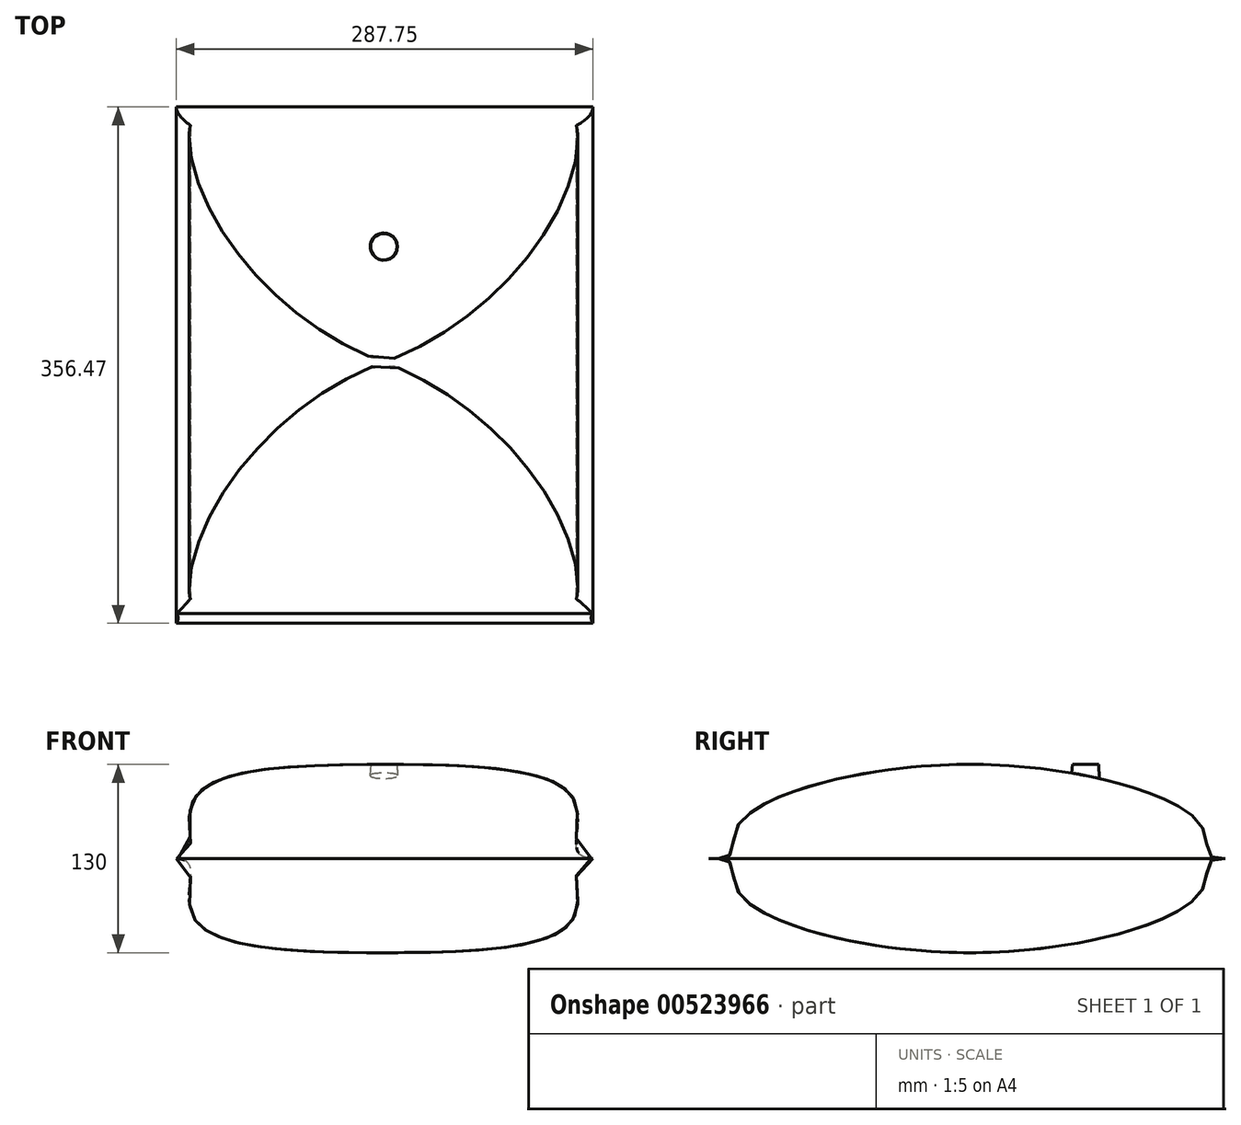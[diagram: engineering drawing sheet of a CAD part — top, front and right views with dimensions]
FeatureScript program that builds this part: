
annotation { "Feature Type Name" : "Feature", "Feature Type Description" : "" }
export const myFeature = defineFeature(function(context is Context, id is Id, definition is map)
    precondition{}
    {
        {
            var Q0;
            Q0=qCreatedBy(makeId("Right.planeOp"),FACE);
            var sketch = newSketch(context, id + "F0", { "sketchPlane" : qUnion([Q0])});
            skLineSegment(sketch, "E0", {"start": v(0, 0) * mm, "end": v(300, 0) * mm});
            skLineSegment(sketch, "E1", {"start": v(0, 0) * mm, "end": v(360, 0) * mm, "construction": true});
            skLineSegment(sketch, "E2", {"start": v(180, 0) * mm, "end": v(180, 198.32) * mm, "construction": true});
            skFitSpline(sketch, "E3", {"points": [v(0, 0) * mm, v(15, 3) * mm, v(19.87, 22.56) * mm, v(180, 65) * mm, v(340.13, 22.56) * mm, v(345, 3) * mm, v(360, 0) * mm], "startDerivative": vector(169.87, -8.58) * mm, "endDerivative": vector(272.86, 0) * mm});
            skFitSpline(sketch, "E4.MirrorCS", {"points": [v(0, 0) * mm, v(15, -3) * mm, v(19.87, -22.56) * mm, v(180, -65) * mm, v(340.13, -22.56) * mm, v(345, -3) * mm, v(360, 0) * mm], "startDerivative": vector(169.87, 8.58) * mm, "endDerivative": vector(272.86, 0) * mm});
            skSolve(sketch);
        }
        {
            var Q0;
            Q0 = qSketchRegion(id + "F0", true);
            extrude(context, id + "F1", {"entities" : qUnion([Q0]), "depth" : 300 * mm, "offsetDistance" : 25 * mm, "symmetric" : true});
        }
        {
            var Q0;
            Q0=qCreatedBy(makeId("Top.planeOp"),FACE);
            var sketch = newSketch(context, id + "F2", { "sketchPlane" : qUnion([Q0])});
            skLineSegment(sketch, "E5", {"start": v(0, -42.79) * mm, "end": v(0, 484.8) * mm, "construction": true});
            skCircle(sketch, "E6", {"center": v(0, 260) * mm, "radius": 12.5 * mm});
            skSolve(sketch);
        }
        {
            var Q0;
            Q0 = qSketchRegion(id + "F2", true);
            extrude(context, id + "F3", {"entities" : qUnion([Q0]), "operationType" : NewBodyOperationType.ADD, "depth" : 65 * mm, "offsetDistance" : 25 * mm, "hasDraft" : true, "draftAngle" : 3 * degree, "draftPullDirection" : true});
        }
        {
            var Q0;
            Q0=qCreatedBy(makeId("Front.planeOp"),FACE);
            var sketch = newSketch(context, id + "F4", { "sketchPlane" : qUnion([Q0])});
            skLineSegment(sketch, "E7", {"start": v(0, 0) * mm, "end": v(0, 80) * mm, "construction": true});
            skLineSegment(sketch, "E8.0", {"start": v(150, 0) * mm, "end": v(-150, 0) * mm, "construction": true});
            skPoint(sketch, "E9.4.internal.snap0", {"position": v(0, 40) * mm});
            skFitSpline(sketch, "E9", {"points": [v(-150, 0) * mm, v(-135, 3.26) * mm, v(-131.8, 40) * mm, v(0, 65) * mm, v(131.8, 40) * mm, v(135, 3.26) * mm, v(150, 0) * mm], "startDerivative": vector(147.27, 0.94) * mm, "endDerivative": vector(58.38, 0) * mm});
            skFitSpline(sketch, "E10.MirrorCS", {"points": [v(-150, 0) * mm, v(-135, -3.26) * mm, v(-131.8, -40) * mm, v(0, -65) * mm, v(131.8, -40) * mm, v(135, -3.26) * mm, v(150, 0) * mm], "startDerivative": vector(147.27, -0.94) * mm, "endDerivative": vector(58.38, 0) * mm});
            skSolve(sketch);
        }
        {
            var Q0;
            {var subQ0=sQuery(id+"F4.wireOp",EDGE,"E10.MirrorCS");var subQ1=sQuery(id+"F4.wireOp",EDGE,"E9");var subQ2=makeQuery(id+"F4.imprint","INTERSECT",VERTEX,{"disambiguationData":[OD(3.0)],"derivedFrom":[subQ1,subQ0]});Q0=makeQuery(id+"F4.imprint","IMPRINT",FACE,{"disambiguationData":[TD([[makeQuery(id+"F4.imprint","IMPRINT",EDGE,{"disambiguationData":[TD([[subQ2,-1.0]])],"derivedFrom":subQ1}),-1.0]])]});}
            var Q1;
            Q1=sQuery(id+"F4.wireOp",EDGE,"E10.MirrorCS");
            var Q2;
            Q2=sQuery(id+"F4.wireOp",EDGE,"E9");
            var Q3;
            {var subQ0=sQuery(id+"F0.wireOp",EDGE,"E4.MirrorCS");var subQ1=sQuery(id+"F0.wireOp",EDGE,"E3");Q3=makeQuery(id+"F1.opExtrude","CAP_VERTEX",VERTEX,{"disambiguationData":[OSD([subQ1,subQ0]),TDD([makeQuery(id+"F0.imprint","INTERSECT",VERTEX,{"disambiguationData":[OD(0.0)],"derivedFrom":[subQ1,subQ0]})])],"isStart":false});}
            extrude(context, id + "F5", {"entities" : qUnion([Q0]), "operationType" : NewBodyOperationType.INTERSECT, "surfaceEntities" : qUnion([Q1, Q2]), "endBound" : BoundingType.UP_TO_VERTEX, "oppositeDirection" : true, "depth" : 337 * mm, "endBoundEntityVertex" : qUnion([Q3]), "offsetDistance" : 25 * mm});
        }
    });
